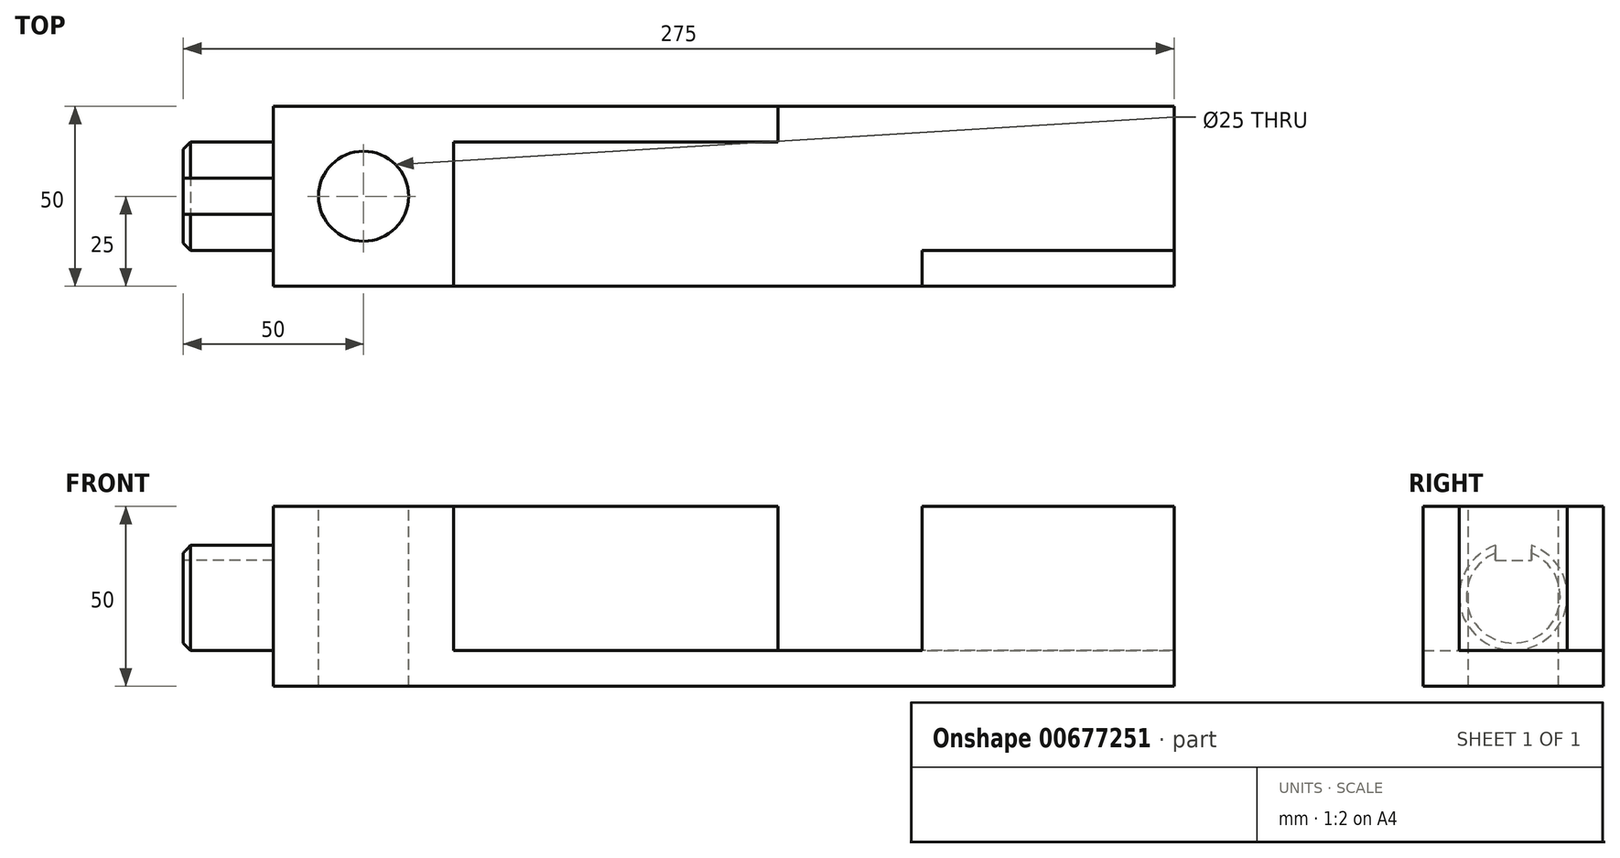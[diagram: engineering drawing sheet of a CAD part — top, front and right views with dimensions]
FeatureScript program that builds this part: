
annotation { "Feature Type Name" : "Feature", "Feature Type Description" : "" }
export const myFeature = defineFeature(function(context is Context, id is Id, definition is map)
    precondition{}
    {
        {
            var Q0;
            Q0=qCreatedBy(makeId("Front.planeOp"),FACE);
            var sketch = newSketch(context, id + "F0", { "sketchPlane" : qUnion([Q0])});
            skLineSegment(sketch, "E0", {"start": v(0, 0) * mm, "end": v(-250, 0) * mm});
            skLineSegment(sketch, "E1", {"start": v(-250, 0) * mm, "end": v(-250, 50) * mm});
            skLineSegment(sketch, "E2", {"start": v(-250, 50) * mm, "end": v(-200, 50) * mm});
            skLineSegment(sketch, "E3", {"start": v(-200, 50) * mm, "end": v(-200, 50) * mm});
            skLineSegment(sketch, "E4", {"start": v(-200, 10) * mm, "end": v(-200, 50) * mm});
            skLineSegment(sketch, "E5", {"start": v(-200, 10) * mm, "end": v(0, 10) * mm});
            skLineSegment(sketch, "E6", {"start": v(0, 10) * mm, "end": v(0, 0) * mm});
            skSolve(sketch);
        }
        {
            var Q0;
            Q0 = qSketchRegion(id + "F0", true);
            extrude(context, id + "F1", {"entities" : qUnion([Q0]), "endBound" : BoundingType.SYMMETRIC, "depth" : 50 * mm, "offsetDistance" : 25 * mm});
        }
        {
            var Q0;
            Q0=makeQuery(id+"F1.opExtrude","SWEPT_FACE",FACE,{"disambiguationData":[OSD([sQuery(id+"F0.wireOp",EDGE,"E5")])]});
            var sketch = newSketch(context, id + "F2", { "sketchPlane" : qUnion([Q0])});
            skLineSegment(sketch, "E7.bottom", {"start": v(-200, 25) * mm, "end": v(-110, 25) * mm});
            skLineSegment(sketch, "E7.top", {"start": v(-200, 15) * mm, "end": v(-110, 15) * mm});
            skLineSegment(sketch, "E7.left", {"start": v(-200, 25) * mm, "end": v(-200, 15) * mm});
            skLineSegment(sketch, "E7.right", {"start": v(-110, 25) * mm, "end": v(-110, 15) * mm});
            skLineSegment(sketch, "E8.bottom", {"start": v(0, -25) * mm, "end": v(-70, -25) * mm});
            skLineSegment(sketch, "E8.top", {"start": v(0, -15) * mm, "end": v(-70, -15) * mm});
            skLineSegment(sketch, "E8.left", {"start": v(0, -25) * mm, "end": v(0, -15) * mm});
            skLineSegment(sketch, "E8.right", {"start": v(-70, -25) * mm, "end": v(-70, -15) * mm});
            skSolve(sketch);
        }
        {
            var Q0;
            Q0 = qSketchRegion(id + "F2", true);
            extrude(context, id + "F3", {"entities" : qUnion([Q0]), "operationType" : NewBodyOperationType.ADD, "depth" : 40 * mm, "offsetDistance" : 25 * mm});
        }
        {
            var Q0;
            Q0=makeQuery(id+"F1.opExtrude","SWEPT_FACE",FACE,{"disambiguationData":[OSD([sQuery(id+"F0.wireOp",EDGE,"E1")])]});
            var sketch = newSketch(context, id + "F4", { "sketchPlane" : qUnion([Q0])});
            skCircle(sketch, "E9", {"center": v(0, 25) * mm, "radius": 15 * mm});
            skLineSegment(sketch, "E10", {"start": v(0, 50) * mm, "end": v(0, 0) * mm, "construction": true});
            skLineSegment(sketch, "E11", {"start": v(-25, 25) * mm, "end": v(25, 25) * mm, "construction": true});
            skSolve(sketch);
        }
        {
            var Q0;
            Q0 = qSketchRegion(id + "F4", true);
            extrude(context, id + "F5", {"entities" : qUnion([Q0]), "operationType" : NewBodyOperationType.ADD, "depth" : 25 * mm, "offsetDistance" : 25 * mm});
        }
        {
            var Q0;
            Q0=makeQuery(id+"F5.opExtrude","CAP_FACE",FACE,{"disambiguationData":[OSD([sQuery(id+"F4.wireOp",EDGE,"E9")])],"isStart":false});
            chamfer(context, id + "F6", {"entities" : qUnion([Q0]), "width" : 2 * mm, "tangentPropagation" : true});
        }
        {
            var Q0;
            Q0=makeQuery(id+"F3.boolean.opBoolean","MERGE",FACE,{"derivedFrom":[makeQuery(id+"F1.opExtrude","SWEPT_FACE",FACE,{"disambiguationData":[OSD([sQuery(id+"F0.wireOp",EDGE,"E2")])]}),makeQuery(id+"F3.opExtrude","CAP_FACE",FACE,{"disambiguationData":[OSD([sQuery(id+"F2.wireOp",EDGE,"E7.bottom"),sQuery(id+"F2.wireOp",EDGE,"E7.top"),sQuery(id+"F2.wireOp",EDGE,"E7.left"),sQuery(id+"F2.wireOp",EDGE,"E7.right")])],"isStart":false})]});
            var sketch = newSketch(context, id + "F7", { "sketchPlane" : qUnion([Q0])});
            skLineSegment(sketch, "E12", {"start": v(-200, 0) * mm, "end": v(-250, 0) * mm, "construction": true});
            skPoint(sketch, "E12.startSnap0", {"position": v(-250, 0) * mm});
            skLineSegment(sketch, "E13", {"start": v(-225, -25) * mm, "end": v(-225, 25) * mm, "construction": true});
            skPoint(sketch, "E14", {"position": v(-225, 0) * mm});
            skSolve(sketch);
        }
        {
            var Q0;
            Q0=sQuery(id+"F7.wireOp",VERTEX,"E14");
            var Q1;
            Q1=makeQuery(id+"F1.opExtrude","SWEPT_BODY",BODY,{"disambiguationData":[OSD([sQuery(id+"F0.wireOp",EDGE,"E0"),sQuery(id+"F0.wireOp",EDGE,"E1"),sQuery(id+"F0.wireOp",EDGE,"E2"),sQuery(id+"F0.wireOp",EDGE,"E4"),sQuery(id+"F0.wireOp",EDGE,"E5"),sQuery(id+"F0.wireOp",EDGE,"E6")])]});
            hole(context, id + "F8", {"style" : HoleStyle.SIMPLE, "endStyle" : HoleEndStyle.THROUGH, "holeDiameter" : 25 * mm, "majorDiameter" : 5 * mm, "isTappedThrough" : true, "tappedDepth" : 12 * mm, "tapClearance" : 3, "locations" : qUnion([Q0]), "scope" : qUnion([Q1])});
        }
        {
            var Q0;
            Q0=makeQuery(id+"F5.opExtrude","CAP_FACE",FACE,{"disambiguationData":[OSD([sQuery(id+"F4.wireOp",EDGE,"E9")])],"isStart":false});
            var sketch = newSketch(context, id + "F9", { "sketchPlane" : qUnion([Q0])});
            skLineSegment(sketch, "E15", {"start": v(0, 38) * mm, "end": v(0, 12) * mm, "construction": true});
            skLineSegment(sketch, "E16", {"start": v(-13, 25) * mm, "end": v(13, 25) * mm, "construction": true});
            skPoint(sketch, "E16.startSnap0", {"position": v(0, 25) * mm});
            skLineSegment(sketch, "E17.bottom", {"start": v(-5, 42) * mm, "end": v(5, 42) * mm});
            skLineSegment(sketch, "E17.top", {"start": v(-5, 35) * mm, "end": v(5, 35) * mm});
            skLineSegment(sketch, "E17.left", {"start": v(-5, 42) * mm, "end": v(-5, 35) * mm});
            skLineSegment(sketch, "E17.right", {"start": v(5, 42) * mm, "end": v(5, 35) * mm});
            skSolve(sketch);
        }
        {
            var Q0;
            {var subQ0=sQuery(id+"F9.wireOp",EDGE,"E17.bottom");Q0=makeQuery(id+"F9.imprint","IMPRINT",FACE,{"disambiguationData":[TD([[makeQuery(id+"F9.imprint","IMPRINT",EDGE,{"derivedFrom":subQ0}),-1.0]])]});}
            var Q1;
            {var subQ0=sQuery(id+"F9.wireOp",EDGE,"E17.top");Q1=makeQuery(id+"F9.imprint","IMPRINT",FACE,{"disambiguationData":[TD([[makeQuery(id+"F9.imprint","IMPRINT",EDGE,{"derivedFrom":subQ0}),1.0]])]});}
            var Q2;
            Q2=makeQuery(id+"F1.opExtrude","SWEPT_FACE",FACE,{"disambiguationData":[OSD([sQuery(id+"F0.wireOp",EDGE,"E1")])]});
            extrude(context, id + "F10", {"entities" : qUnion([Q0, Q1]), "operationType" : NewBodyOperationType.REMOVE, "endBound" : BoundingType.UP_TO_SURFACE, "oppositeDirection" : true, "depth" : 25 * mm, "endBoundEntityFace" : qUnion([Q2]), "offsetDistance" : 25 * mm});
        }
    });
